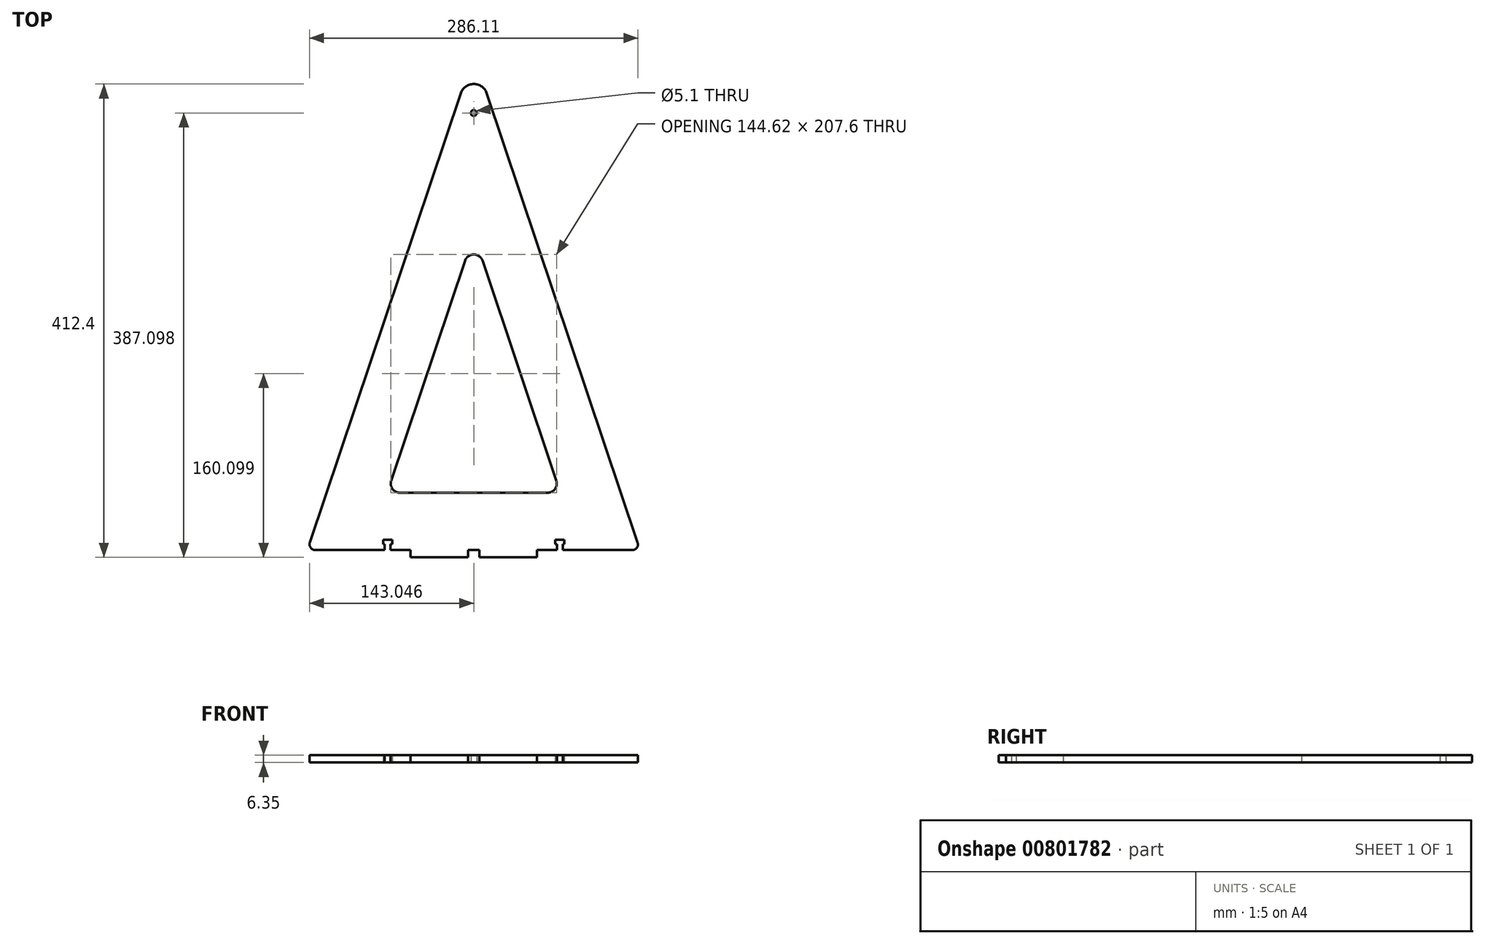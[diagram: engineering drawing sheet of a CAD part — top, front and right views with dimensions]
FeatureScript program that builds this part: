
annotation { "Feature Type Name" : "Feature", "Feature Type Description" : "" }
export const myFeature = defineFeature(function(context is Context, id is Id, definition is map)
    precondition{}
    {
        {
            var Q0;
            Q0=qCreatedBy(makeId("Top.planeOp"),FACE);
            var sketch = newSketch(context, id + "F0", { "sketchPlane" : qUnion([Q0])});
            skLineSegment(sketch, "E0", {"start": v(-140.33, -45.14) * mm, "end": v(-8.92, 346.2) * mm});
            skLineSegment(sketch, "E1", {"start": v(-135.6, -51.73) * mm, "end": v(-52.54, -51.73) * mm});
            skLineSegment(sketch, "E2", {"start": v(-52.54, -51.73) * mm, "end": v(-52.54, -58.03) * mm});
            skLineSegment(sketch, "E3", {"start": v(-52.54, -58.03) * mm, "end": v(-2.54, -58.03) * mm});
            skLineSegment(sketch, "E4", {"start": v(-2.54, -58.03) * mm, "end": v(-2.54, -51.73) * mm});
            skLineSegment(sketch, "E5", {"start": v(-2.54, -51.73) * mm, "end": v(2.46, -51.73) * mm});
            skLineSegment(sketch, "E6.top", {"start": v(-75.1, -42.73) * mm, "end": v(-70, -42.73) * mm});
            skLineSegment(sketch, "E6.left", {"start": v(-75.1, -51.73) * mm, "end": v(-75.1, -42.73) * mm, "construction": true});
            skLineSegment(sketch, "E6.right", {"start": v(-70, -51.73) * mm, "end": v(-70, -42.73) * mm, "construction": true});
            skLineSegment(sketch, "E7.bottom", {"start": v(-72.54, -42.73) * mm, "end": v(-76.54, -42.73) * mm});
            skLineSegment(sketch, "E7.top", {"start": v(-72.54, -46.73) * mm, "end": v(-76.54, -46.73) * mm, "construction": true});
            skLineSegment(sketch, "E7.left", {"start": v(-72.54, -46.73) * mm, "end": v(-72.54, -42.73) * mm, "construction": true});
            skLineSegment(sketch, "E7.right", {"start": v(-76.54, -46.73) * mm, "end": v(-76.54, -42.73) * mm});
            skLineSegment(sketch, "E8.MirrorCS", {"start": v(-68.54, -46.73) * mm, "end": v(-68.54, -42.73) * mm});
            skLineSegment(sketch, "E9.MirrorCS", {"start": v(-72.54, -46.73) * mm, "end": v(-68.54, -46.73) * mm, "construction": true});
            skLineSegment(sketch, "E10.MirrorCS", {"start": v(-72.54, -42.73) * mm, "end": v(-68.54, -42.73) * mm});
            skLineSegment(sketch, "E11.MirrorCS", {"start": v(145.26, -45.2) * mm, "end": v(13.83, 346.2) * mm});
            skLineSegment(sketch, "E12.MirrorCS", {"start": v(77.46, -46.73) * mm, "end": v(77.46, -42.73) * mm, "construction": true});
            skLineSegment(sketch, "E13.MirrorCS", {"start": v(80, -42.73) * mm, "end": v(74.9, -42.73) * mm});
            skLineSegment(sketch, "E14.MirrorCS", {"start": v(81.46, -46.73) * mm, "end": v(81.46, -42.73) * mm});
            skLineSegment(sketch, "E15.MirrorCS", {"start": v(77.46, -46.73) * mm, "end": v(81.46, -46.73) * mm, "construction": true});
            skLineSegment(sketch, "E16.MirrorCS", {"start": v(77.46, -42.73) * mm, "end": v(81.46, -42.73) * mm});
            skLineSegment(sketch, "E17.MirrorCS", {"start": v(73.46, -46.73) * mm, "end": v(73.46, -42.73) * mm});
            skLineSegment(sketch, "E18.MirrorCS", {"start": v(77.46, -46.73) * mm, "end": v(73.46, -46.73) * mm, "construction": true});
            skLineSegment(sketch, "E19.MirrorCS", {"start": v(77.46, -42.73) * mm, "end": v(73.46, -42.73) * mm});
            skLineSegment(sketch, "E20.MirrorCS", {"start": v(7.46, -51.73) * mm, "end": v(2.46, -51.73) * mm});
            skLineSegment(sketch, "E21.MirrorCS", {"start": v(74.9, -51.73) * mm, "end": v(74.9, -42.73) * mm, "construction": true});
            skLineSegment(sketch, "E22.MirrorCS", {"start": v(80, -51.73) * mm, "end": v(80, -42.73) * mm, "construction": true});
            skLineSegment(sketch, "E23.MirrorCS", {"start": v(7.46, -58.03) * mm, "end": v(7.46, -51.73) * mm});
            skLineSegment(sketch, "E24.MirrorCS", {"start": v(57.46, -51.73) * mm, "end": v(57.46, -58.03) * mm});
            skLineSegment(sketch, "E25.MirrorCS", {"start": v(140.57, -51.73) * mm, "end": v(57.46, -51.73) * mm});
            skLineSegment(sketch, "E26.MirrorCS", {"start": v(57.46, -58.03) * mm, "end": v(7.46, -58.03) * mm});
            skCircle(sketch, "E27", {"center": v(2.46, 85.27) * mm, "radius": 2.55 * mm});
            skLineSegment(sketch, "E28", {"start": v(2.46, -1.73) * mm, "end": v(-61.88, -1.73) * mm});
            skLineSegment(sketch, "E29", {"start": v(-69.47, 8.81) * mm, "end": v(-5.13, 200.42) * mm});
            skLineSegment(sketch, "E30.MirrorCS", {"start": v(74.38, 8.81) * mm, "end": v(10.04, 200.42) * mm});
            skLineSegment(sketch, "E31.MirrorCS", {"start": v(2.46, -1.73) * mm, "end": v(66.8, -1.73) * mm});
            skCircle(sketch, "E32", {"center": v(2.46, 329.07) * mm, "radius": 2.55 * mm});
            skPoint(sketch, "E33.visualSharp", {"position": v(2.46, 380.07) * mm});
            skArc(sketch, "E33.filletArc", {"start": v(13.83, 346.2) * mm, "mid": v(2.46, 354.37) * mm, "end": v(-8.92, 346.2) * mm});
            skPoint(sketch, "E34.visualSharp", {"position": v(-73, -1.73) * mm});
            skArc(sketch, "E34.filletArc", {"start": v(-69.47, 8.81) * mm, "mid": v(-68.38, 1.6) * mm, "end": v(-61.88, -1.73) * mm});
            skPoint(sketch, "E35.visualSharp", {"position": v(77.92, -1.73) * mm});
            skArc(sketch, "E35.filletArc", {"start": v(66.8, -1.73) * mm, "mid": v(73.3, 1.6) * mm, "end": v(74.38, 8.81) * mm});
            skPoint(sketch, "E36.visualSharp", {"position": v(2.46, 223) * mm});
            skArc(sketch, "E36.filletArc", {"start": v(10.04, 200.42) * mm, "mid": v(2.46, 205.87) * mm, "end": v(-5.13, 200.42) * mm});
            skPoint(sketch, "E37.visualSharp", {"position": v(-142.54, -51.73) * mm});
            skPoint(sketch, "E38.visualSharp", {"position": v(147.46, -51.73) * mm});
            skArc(sketch, "E38.filletArc", {"start": v(140.57, -51.73) * mm, "mid": v(144.59, -49.67) * mm, "end": v(145.26, -45.2) * mm});
            skArc(sketch, "E39.filletArc", {"start": v(-140.33, -45.14) * mm, "mid": v(-139.65, -49.65) * mm, "end": v(-135.6, -51.73) * mm});
            skLineSegment(sketch, "E40", {"start": v(-76.54, -46.73) * mm, "end": v(-75.1, -46.73) * mm});
            skLineSegment(sketch, "E41", {"start": v(-75.1, -46.73) * mm, "end": v(-75.1, -51.73) * mm});
            skLineSegment(sketch, "E42", {"start": v(-68.54, -46.73) * mm, "end": v(-70, -46.73) * mm});
            skLineSegment(sketch, "E43", {"start": v(-70, -46.73) * mm, "end": v(-70, -51.73) * mm});
            skLineSegment(sketch, "E44", {"start": v(73.46, -46.73) * mm, "end": v(74.9, -46.73) * mm});
            skLineSegment(sketch, "E45", {"start": v(74.9, -46.73) * mm, "end": v(74.9, -51.73) * mm});
            skLineSegment(sketch, "E46", {"start": v(81.46, -46.73) * mm, "end": v(80, -46.73) * mm});
            skLineSegment(sketch, "E47", {"start": v(80, -46.73) * mm, "end": v(80, -51.73) * mm});
            skSolve(sketch);
        }
        {
            var Q0;
            Q0=makeQuery(id+"F0.imprint","IMPRINT",FACE,{"disambiguationData":[TD([[makeQuery(id+"F0.imprint","IMPRINT",EDGE,{"derivedFrom":sQuery(id+"F0.wireOp",EDGE,"E0")}),-1.0]])]});
            extrude(context, id + "F1", {"entities" : qUnion([Q0]), "depth" : 6.35 * mm, "offsetDistance" : 25 * mm});
        }
    });
